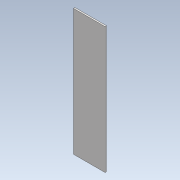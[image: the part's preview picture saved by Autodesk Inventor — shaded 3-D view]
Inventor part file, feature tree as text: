
AUTODESK INVENTOR PART (.ipt)
format: ipt  version: 2021 (Build 250183000, 183)  size: 75,776 bytes
history: native  units: in
note: dims shown in document units (in); Inventor stores cm internally (conversion verified against a paired STEP export)
features: extrude x1, sketch x1
ambient origin geometry x8: Origin, YZ Plane, XZ Plane, XY Plane, X Axis, Y Axis, Z Axis, Center Point
bodies: Solid1 (feature_tree)
feature tree (2):
  extrude  "Extrusion1"  Depth=4.3in
  sketch  "Sketch1"  dims[d0=1.0722in d1=4.3in d2=0.05in d3=0.0in]
